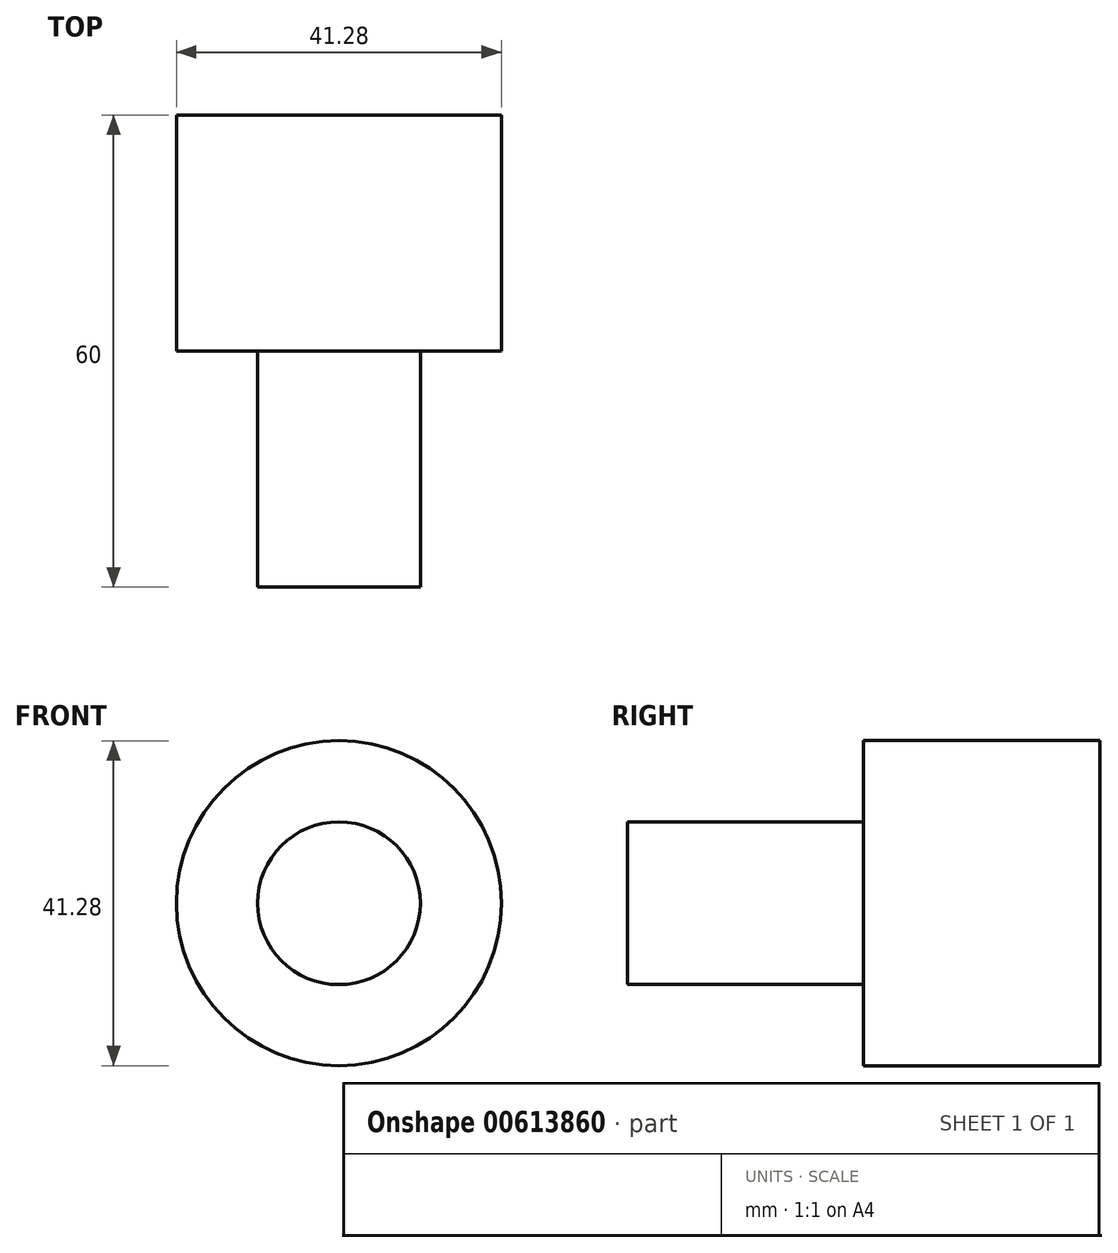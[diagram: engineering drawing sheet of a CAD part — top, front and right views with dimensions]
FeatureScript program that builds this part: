
annotation { "Feature Type Name" : "Feature", "Feature Type Description" : "" }
export const myFeature = defineFeature(function(context is Context, id is Id, definition is map)
    precondition{}
    {
        {
            var Q0;
            Q0=qCreatedBy(makeId("Front.planeOp"),FACE);
            var sketch = newSketch(context, id + "F0", { "sketchPlane" : qUnion([Q0])});
            skCircle(sketch, "E0", {"center": v(0, 0) * mm, "radius": 20.64 * mm});
            skSolve(sketch);
        }
        {
            var Q0;
            Q0=qCreatedBy(makeId("Front.planeOp"),FACE);
            var sketch = newSketch(context, id + "F1", { "sketchPlane" : qUnion([Q0])});
            skCircle(sketch, "E1", {"center": v(0, 0) * mm, "radius": 10.34 * mm});
            skSolve(sketch);
        }
        {
            var Q0;
            Q0 = qSketchRegion(id + "F1", true);
            extrude(context, id + "F2", {"entities" : qUnion([Q0]), "depth" : 60 * mm, "offsetDistance" : 25 * mm});
        }
        {
            var Q0;
            Q0 = qSketchRegion(id + "F0", true);
            extrude(context, id + "F3", {"entities" : qUnion([Q0]), "operationType" : NewBodyOperationType.ADD, "depth" : 30 * mm, "offsetDistance" : 25 * mm});
        }
    });
